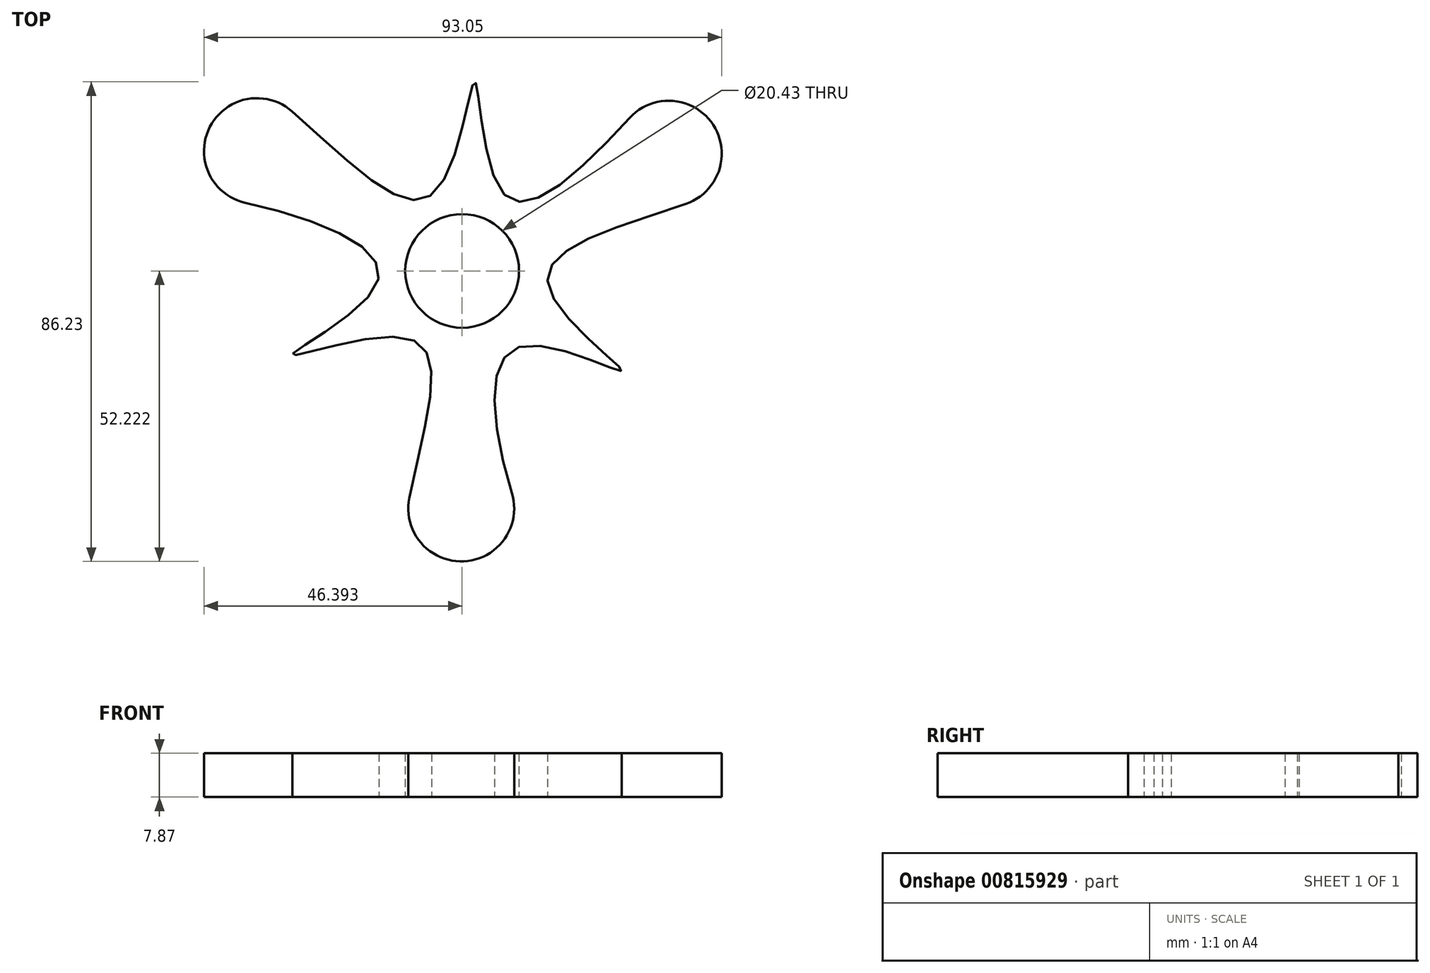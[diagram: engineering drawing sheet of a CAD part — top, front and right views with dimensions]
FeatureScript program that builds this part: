
annotation { "Feature Type Name" : "Feature", "Feature Type Description" : "" }
export const myFeature = defineFeature(function(context is Context, id is Id, definition is map)
    precondition{}
    {
        {
            var Q0;
            Q0=qCreatedBy(makeId("Top.planeOp"),FACE);
            var sketch = newSketch(context, id + "F0", { "sketchPlane" : qUnion([Q0])});
            skCircle(sketch, "E0", {"center": v(-116.27, 69.81) * mm, "radius": 9.53 * mm});
            skCircle(sketch, "E1", {"center": v(-42.28, 69.35) * mm, "radius": 9.53 * mm});
            skCircle(sketch, "E2", {"center": v(-79.57, 5.58) * mm, "radius": 9.53 * mm});
            skCircle(sketch, "E3", {"center": v(-79.4, 48.27) * mm, "radius": 10.22 * mm});
            skLineSegment(sketch, "E4", {"start": v(-116.27, 69.81) * mm, "end": v(-79.4, 48.27) * mm});
            skLineSegment(sketch, "E5", {"start": v(-42.28, 69.35) * mm, "end": v(-79.4, 48.27) * mm});
            skLineSegment(sketch, "E6", {"start": v(-79.57, 5.58) * mm, "end": v(-79.4, 48.27) * mm});
            skFitSpline(sketch, "E7", {"points": [v(-118.37, 60.52) * mm, v(-94.57, 46.42) * mm, v(-109.93, 33.22) * mm, v(-88.77, 36.03) * mm, v(-88.9, 7.47) * mm], "startDerivative": vector(135.12, -30.6) * mm, "endDerivative": vector(-31.8, -156.95) * mm});
            skFitSpline(sketch, "E8", {"points": [v(-70.43, 8.24) * mm, v(-68.82, 34.7) * mm, v(-50.73, 30.34) * mm, v(-63.86, 45.2) * mm, v(-39.24, 60.32) * mm], "startDerivative": vector(-41.08, 132.31) * mm, "endDerivative": vector(151.79, 51.05) * mm});
            skFitSpline(sketch, "E9", {"points": [v(-49.22, 75.88) * mm, v(-71.77, 61.95) * mm, v(-77.15, 82.28) * mm, v(-84.26, 62.51) * mm, v(-109.96, 76.95) * mm], "startDerivative": vector(-94.06, -101.72) * mm, "endDerivative": vector(-120.02, 106.02) * mm});
            skSolve(sketch);
        }
        {
            var Q0;
            Q0 = qSketchRegion(id + "F0", true);
            extrude(context, id + "F1", {"entities" : qUnion([Q0]), "depth" : 7.87 * mm, "offsetDistance" : 25.4 * mm});
        }
    });
